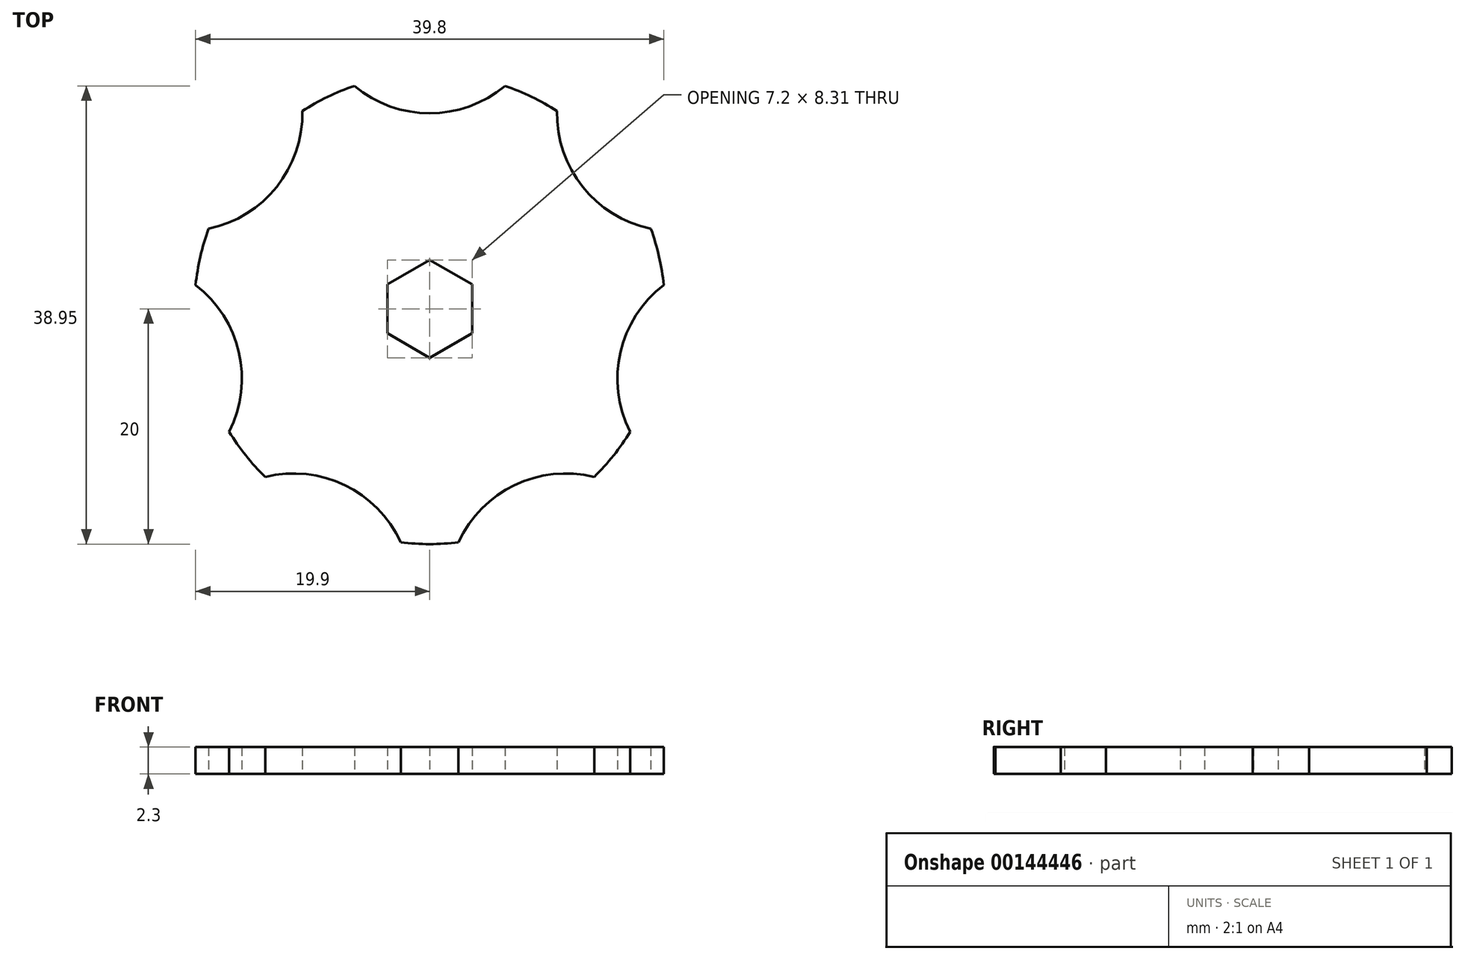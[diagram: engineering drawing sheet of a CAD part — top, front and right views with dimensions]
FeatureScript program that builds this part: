
annotation { "Feature Type Name" : "Feature", "Feature Type Description" : "" }
export const myFeature = defineFeature(function(context is Context, id is Id, definition is map)
    precondition{}
    {
        {
            var Q0;
            Q0=qCreatedBy(makeId("Top.planeOp"),FACE);
            var sketch = newSketch(context, id + "F0", { "sketchPlane" : qUnion([Q0])});
            skCircle(sketch, "E0.cCircle", {"center": v(0, 0) * mm, "radius": 3.6 * mm, "construction": true});
            skLineSegment(sketch, "E0.0", {"start": v(3.6, 2.08) * mm, "end": v(3.6, -2.08) * mm});
            skLineSegment(sketch, "E0.1", {"start": v(3.6, -2.08) * mm, "end": v(0, -4.16) * mm});
            skLineSegment(sketch, "E0.2", {"start": v(0, -4.16) * mm, "end": v(-3.6, -2.08) * mm});
            skLineSegment(sketch, "E0.3", {"start": v(-3.6, -2.08) * mm, "end": v(-3.6, 2.08) * mm});
            skLineSegment(sketch, "E0.4", {"start": v(-3.6, 2.08) * mm, "end": v(0, 4.16) * mm});
            skLineSegment(sketch, "E0.5", {"start": v(0, 4.16) * mm, "end": v(3.6, 2.08) * mm});
            skPoint(sketch, "E0.0.midPoint", {"position": v(3.6, 0) * mm});
            skCircle(sketch, "E1", {"center": v(0, 0) * mm, "radius": 20 * mm});
            skSolve(sketch);
        }
        {
            var Q0;
            Q0=makeQuery(id+"F0.imprint","IMPRINT",FACE,{"disambiguationData":[TD([[makeQuery(id+"F0.imprint","IMPRINT",EDGE,{"derivedFrom":sQuery(id+"F0.wireOp",EDGE,"E0.0")}),1.0]])]});
            extrude(context, id + "F1", {"entities" : qUnion([Q0]), "depth" : 2.3 * mm});
        }
        {
            var Q0;
            Q0=qCreatedBy(makeId("Top.planeOp"),FACE);
            var sketch = newSketch(context, id + "F2", { "sketchPlane" : qUnion([Q0])});
            skCircle(sketch, "E2", {"center": v(0, 26.63) * mm, "radius": 10 * mm});
            skCircle(sketch, "E3.1.0", {"center": v(-20.82, 16.6) * mm, "radius": 10 * mm});
            skCircle(sketch, "E3.2.0", {"center": v(-25.97, -5.93) * mm, "radius": 10 * mm});
            skCircle(sketch, "E3.3.0", {"center": v(-11.56, -24) * mm, "radius": 10 * mm});
            skCircle(sketch, "E3.4.0", {"center": v(11.56, -24) * mm, "radius": 10 * mm});
            skCircle(sketch, "E3.5.0", {"center": v(25.97, -5.93) * mm, "radius": 10 * mm});
            skCircle(sketch, "E3.6.0", {"center": v(20.82, 16.6) * mm, "radius": 10 * mm});
            skPoint(sketch, "E3.center", {"position": v(0, 0) * mm});
            skSolve(sketch);
        }
        {
            var Q0;
            Q0 = qSketchRegion(id + "F2", true);
            extrude(context, id + "F3", {"entities" : qUnion([Q0]), "operationType" : NewBodyOperationType.REMOVE, "endBound" : BoundingType.THROUGH_ALL, "depth" : 25 * mm});
        }
    });
